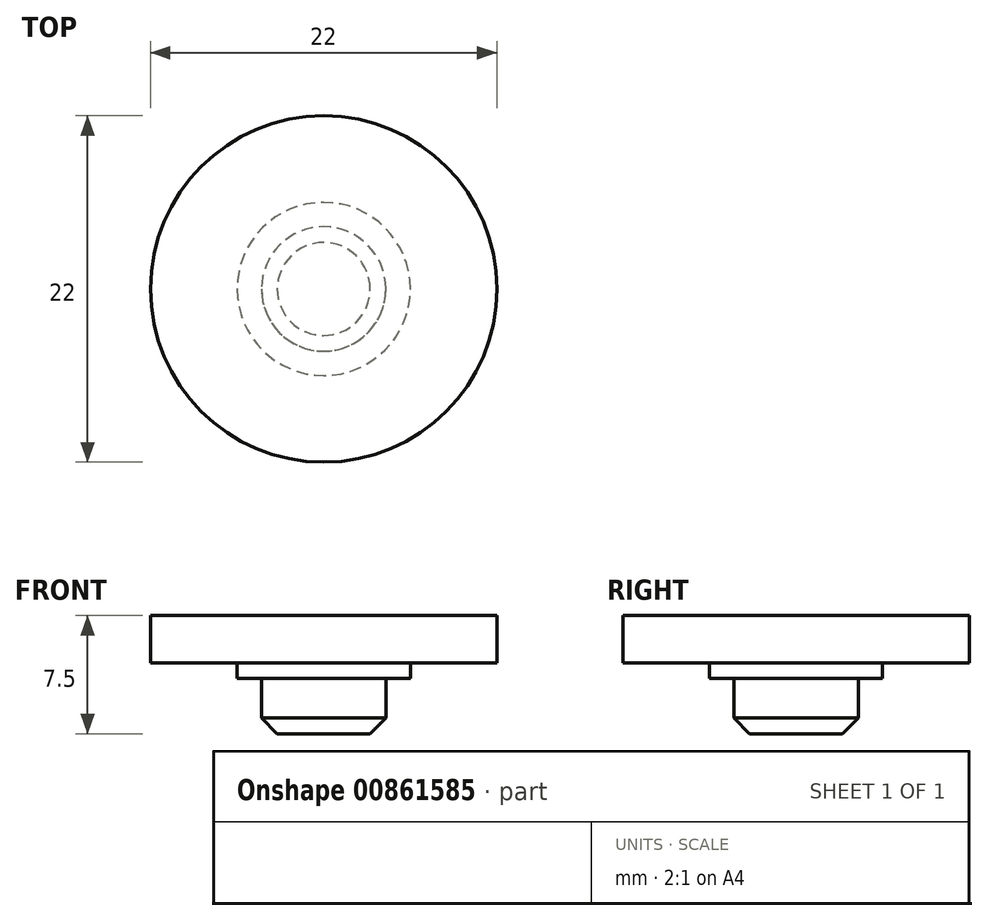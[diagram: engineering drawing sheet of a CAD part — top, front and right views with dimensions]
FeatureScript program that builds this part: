
annotation { "Feature Type Name" : "Feature", "Feature Type Description" : "" }
export const myFeature = defineFeature(function(context is Context, id is Id, definition is map)
    precondition{}
    {
        {
            var Q0;
            Q0=qCreatedBy(makeId("Front.planeOp"),FACE);
            var sketch = newSketch(context, id + "F0", { "sketchPlane" : qUnion([Q0])});
            skLineSegment(sketch, "E0", {"start": v(0, 0) * mm, "end": v(0, 7.5) * mm});
            skLineSegment(sketch, "E1", {"start": v(0, 7.5) * mm, "end": v(-11, 7.5) * mm});
            skLineSegment(sketch, "E2", {"start": v(-11, 7.5) * mm, "end": v(-11, 4.5) * mm});
            skLineSegment(sketch, "E3", {"start": v(-11, 4.5) * mm, "end": v(-5.5, 4.5) * mm});
            skLineSegment(sketch, "E4", {"start": v(-5.5, 4.5) * mm, "end": v(-5.5, 3.5) * mm});
            skLineSegment(sketch, "E5", {"start": v(-5.5, 3.5) * mm, "end": v(-3.95, 3.5) * mm});
            skLineSegment(sketch, "E6", {"start": v(-3.95, 3.5) * mm, "end": v(-3.95, 0) * mm});
            skLineSegment(sketch, "E7", {"start": v(-3.95, 0) * mm, "end": v(0, 0) * mm});
            skSolve(sketch);
        }
        {
            var Q0;
            Q0=makeQuery(id+"F0.imprint","IMPRINT",FACE,{"disambiguationData":[TD([[makeQuery(id+"F0.imprint","IMPRINT",EDGE,{"derivedFrom":sQuery(id+"F0.wireOp",EDGE,"E0")}),1.0]])]});
            var Q1;
            Q1=sQuery(id+"F0.wireOp",EDGE,"E0");
            revolve(context, id + "F1", {"surfaceOperationType" : NewSurfaceOperationType.NEW, "entities" : qUnion([Q0]), "axis" : qUnion([Q1]), "revolveType" : RevolveType.FULL});
        }
        {
            var Q0;
            Q0=makeQuery(id+"F1.opRevolve","SWEPT_EDGE",EDGE,{"disambiguationData":[OSD([sQuery(id+"F0.wireOp",EDGE,"E6"),sQuery(id+"F0.wireOp",EDGE,"E7")])]});
            chamfer(context, id + "F2", {"entities" : qUnion([Q0]), "width" : 1 * mm, "tangentPropagation" : true});
        }
    });
